# Revit family: AP-5152
name_source: partatom
category: Communication Devices
revit_build: Autodesk Revit Architecture 2012 (Build: 20110309_2315(x64)
units: mm (PartAtom-declared; Revit-internal decimal feet)

## types (1)
- AP-5152
    Coverage Horizontal = 75.00°
    Coverage Vertical = 75.00°
    Default Elevation = 0 mm
    Depth = 386 mm
    Description = 15-inch, Two-way Trapezoidal Enclosure with 75-degree Axisymmetric Coverage
15-inch, Two-way Trapezoidal Enclosure with 75-degree Axisymmetric Coverage
    Grill Apex to Apex = 346 mm
    Grill Height = 783 mm
    Grill Rear Offset from Front = 49 mm
    Height = 813 mm
    Impedance = 8
    Manufacturer = QSC Audio Products, LLC
    Manufacturer URL = www.qscaudio.com
    Model = AP-5152
    Power Handling = 625
    Product Documentation Link = http://qscmarketing.com
    Product Page URL = http://www.qsc.com
    Rear Face Width = 228 mm
    Regulatory Compliance = RoHS
    SPL Max = 129
    Sensitivity = 96
    Taper Offset from Front = 69 mm
    URL = http://www.qsc.com
    Weight Dimensional (kg) = 41
    Weight Dimensional (lb) = 90
    Weight Product (kg) = 36.2
    Weight Product (lb) = 80
    Width = 445 mm

## geometry (parser evidence)
native form markers: Sweep x1
no freeform markers — native parametric forms only
